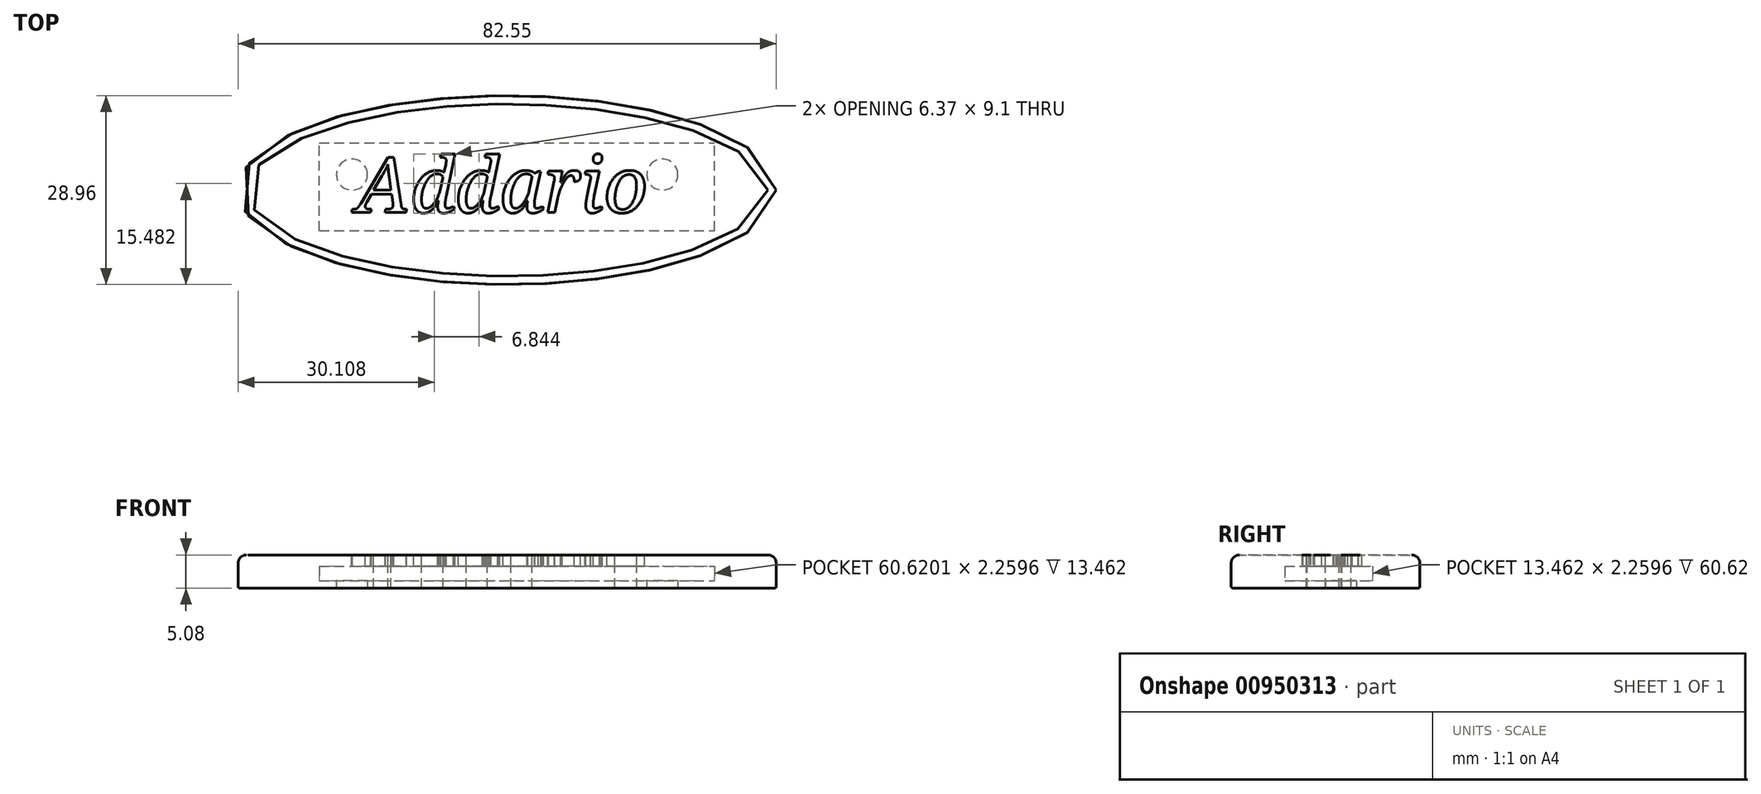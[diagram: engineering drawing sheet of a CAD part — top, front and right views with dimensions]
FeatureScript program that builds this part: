
annotation { "Feature Type Name" : "Feature", "Feature Type Description" : "" }
export const myFeature = defineFeature(function(context is Context, id is Id, definition is map)
    precondition{}
    {
        {
            var Q0;
            Q0=qCreatedBy(makeId("Top.planeOp"),FACE);
            var sketch = newSketch(context, id + "F0", { "sketchPlane" : qUnion([Q0])});
            skEllipse(sketch, "E0", {"center": v(0, 0) * mm, "majorRadius": 41.28 * mm, "minorRadius": 14.48 * mm, "majorAxis": v(1, 0)});
            skPoint(sketch, "E1.centerSnap0", {"position": v(-41.28, 0) * mm});
            skCircle(sketch, "E2", {"center": v(23.81, 2.38) * mm, "radius": 2.38 * mm});
            skPoint(sketch, "E2.centerSnap0", {"position": v(41.28, 0) * mm});
            skCircle(sketch, "E3", {"center": v(-23.81, 2.38) * mm, "radius": 2.38 * mm});
            skPoint(sketch, "E4", {"position": v(0, 14.48) * mm});
            skPoint(sketch, "E5", {"position": v(0, -14.48) * mm});
            skSolve(sketch);
        }
        {
            var Q0;
            Q0=makeQuery(id+"F0.imprint","IMPRINT",FACE,{"disambiguationData":[TD([[makeQuery(id+"F0.imprint","IMPRINT",EDGE,{"derivedFrom":sQuery(id+"F0.wireOp",EDGE,"E0")}),1.0]])]});
            var Q1;
            Q1=makeQuery(id+"F0.imprint","IMPRINT",FACE,{"disambiguationData":[TD([[makeQuery(id+"F0.imprint","IMPRINT",EDGE,{"derivedFrom":sQuery(id+"F0.wireOp",EDGE,"E3")}),1.0]])]});
            var Q2;
            Q2=makeQuery(id+"F0.imprint","IMPRINT",FACE,{"disambiguationData":[TD([[makeQuery(id+"F0.imprint","IMPRINT",EDGE,{"derivedFrom":sQuery(id+"F0.wireOp",EDGE,"E2")}),1.0]])]});
            extrude(context, id + "F1", {"entities" : qUnion([Q0, Q1, Q2]), "depth" : 5.08 * mm, "offsetDistance" : 25.4 * mm});
        }
        {
            var Q0;
            Q0=makeQuery(id+"F1.opExtrude","CAP_EDGE",EDGE,{"disambiguationData":[OSD([sQuery(id+"F0.wireOp",EDGE,"E0")])],"isStart":false});
            fillet(context, id + "F2", {"entities" : qUnion([Q0]), "radius" : 1.27 * mm, "tangentPropagation" : true, "allowEdgeOverflow" : false});
        }
        {
            var Q0;
            Q0=makeQuery(id+"F1.opExtrude","CAP_FACE",FACE,{"disambiguationData":[OSD([sQuery(id+"F0.wireOp",EDGE,"E0")])],"isStart":false});
            var sketch = newSketch(context, id + "F3", { "sketchPlane" : qUnion([Q0])});
            skText(sketch, "E6", { "text": "Addario", "fontName": "NotoSerif-Italic.ttf"});
            const initialGuessF3  = {"E6": [-0.02319, -0.00343, 1, 0, 0.00851]};
            skSetInitialGuess(sketch, initialGuessF3);
            skSolve(sketch);
        }
        {
            var Q0;
            Q0 = qSketchRegion(id + "F3", true);
            extrude(context, id + "F4", {"entities" : qUnion([Q0]), "operationType" : NewBodyOperationType.REMOVE, "oppositeDirection" : true, "depth" : 2.54 * mm, "offsetDistance" : 25.4 * mm});
        }
        {
            var Q0;
            Q0=makeQuery(id+"F0.imprint","IMPRINT",FACE,{"disambiguationData":[TD([[makeQuery(id+"F0.imprint","IMPRINT",EDGE,{"derivedFrom":sQuery(id+"F0.wireOp",EDGE,"E3")}),1.0]])]});
            var Q1;
            Q1=makeQuery(id+"F0.imprint","IMPRINT",FACE,{"disambiguationData":[TD([[makeQuery(id+"F0.imprint","IMPRINT",EDGE,{"derivedFrom":sQuery(id+"F0.wireOp",EDGE,"E2")}),1.0]])]});
            var Q2;
            Q2=sQuery(id+"F0.wireOp",EDGE,"E3");
            var Q3;
            Q3=sQuery(id+"F0.wireOp",EDGE,"E2");
            extrude(context, id + "F5", {"entities" : qUnion([Q0, Q1]), "operationType" : NewBodyOperationType.REMOVE, "surfaceEntities" : qUnion([Q2, Q3]), "depth" : 2.54 * mm, "offsetDistance" : 25.4 * mm});
        }
        {
            var Q0;
            Q0=makeQuery(id+"F1.opExtrude","CAP_EDGE",EDGE,{"disambiguationData":[OSD([sQuery(id+"F0.wireOp",EDGE,"E0")])],"isStart":true});
            fillet(context, id + "F6", {"entities" : qUnion([Q0]), "radius" : 0.25 * mm, "tangentPropagation" : true, "allowEdgeOverflow" : false});
        }
        {
            var Q0;
            Q0=sQuery(id+"F0.wireOp",VERTEX,"E0.center");
            var Q1;
            Q1=sQuery(id+"F0.wireOp",VERTEX,"E4");
            cPlane(context, id + "F7", {"entities" : qUnion([Q0, Q1]), "cplaneType" : CPlaneType.MID_PLANE, "offset" : 25.4 * mm, "width" : 152.4 * mm, "height" : 152.4 * mm});
        }
        {
            var Q0;
            Q0=qCreatedBy(id+"F7.planeOp",FACE);
            var sketch = newSketch(context, id + "F8", { "sketchPlane" : qUnion([Q0])});
            skLineSegment(sketch, "E7.bottom", {"start": v(28.81, 3.37) * mm, "end": v(-31.8, 3.37) * mm});
            skLineSegment(sketch, "E7.top", {"start": v(28.81, 1.1) * mm, "end": v(-31.8, 1.1) * mm});
            skLineSegment(sketch, "E7.left", {"start": v(28.81, 3.37) * mm, "end": v(28.81, 1.1) * mm});
            skLineSegment(sketch, "E7.right", {"start": v(-31.8, 3.37) * mm, "end": v(-31.8, 1.1) * mm});
            skSolve(sketch);
        }
        {
            var Q0;
            Q0 = qSketchRegion(id + "F8", true);
            extrude(context, id + "F9", {"entities" : qUnion([Q0]), "operationType" : NewBodyOperationType.REMOVE, "oppositeDirection" : true, "depth" : 13.46 * mm, "offsetDistance" : 25.4 * mm});
        }
        {
            var Q0;
            Q0=makeQuery(id+"F3.imprint","IMPRINT",FACE,{"disambiguationData":[TD([[makeQuery(id+"F3.imprint","IMPRINT",EDGE,{"derivedFrom":sQuery(id+"F3.wireOp",EDGE,"E6.sketch_text.stroke-24")}),1.0]])]});
            var Q1;
            Q1=makeQuery(id+"F3.imprint","IMPRINT",FACE,{"disambiguationData":[TD([[makeQuery(id+"F3.imprint","IMPRINT",EDGE,{"derivedFrom":sQuery(id+"F3.wireOp",EDGE,"E6.sketch_text.stroke-51")}),1.0]])]});
            var Q2;
            Q2=makeQuery(id+"F3.imprint","IMPRINT",FACE,{"disambiguationData":[TD([[makeQuery(id+"F3.imprint","IMPRINT",EDGE,{"derivedFrom":sQuery(id+"F3.wireOp",EDGE,"E6.sketch_text.stroke-80")}),1.0]])]});
            var Q3;
            Q3=makeQuery(id+"F3.imprint","IMPRINT",FACE,{"disambiguationData":[TD([[makeQuery(id+"F3.imprint","IMPRINT",EDGE,{"derivedFrom":sQuery(id+"F3.wireOp",EDGE,"E6.sketch_text.stroke-104")}),1.0]])]});
            var Q4;
            Q4=makeQuery(id+"F3.imprint","IMPRINT",FACE,{"disambiguationData":[TD([[makeQuery(id+"F3.imprint","IMPRINT",EDGE,{"derivedFrom":sQuery(id+"F3.wireOp",EDGE,"E6.sketch_text.stroke-157")}),1.0]])]});
            extrude(context, id + "F10", {"entities" : qUnion([Q0, Q1, Q2, Q3, Q4]), "oppositeDirection" : true, "depth" : 5.08 * mm, "offsetDistance" : 25.4 * mm});
        }
    });
